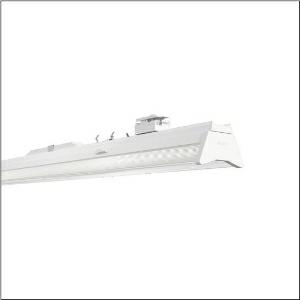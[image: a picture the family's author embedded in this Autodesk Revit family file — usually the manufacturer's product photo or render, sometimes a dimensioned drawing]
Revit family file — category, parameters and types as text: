
# Revit family: licross_r__21_performance_mo_51td16vn445g_3318
name_source: partatom
category: Lighting Fixtures
units: mm (PartAtom-declared; Revit-internal decimal feet)

## family parameters
Cut with Voids When Loaded = No
Host = Face
Light Source = No
Part Type = Normal
Room Calculation Point = No
Round Connector Dimension = Use Diameter
Shared = No

## types (1)
- --- (1 x LED, 4500 lm, 24.2 W, 4000K)
    Apparent Load = 24 VA
    CIE Flux Codes = 66 88 96 79 100
    Color Rendering = 80
    Color Temperature = 4000K
    Default Elevation = 1800 mm
    Description = Licross® 21 Performance MO, luminaire insert, of sheet steel, galvanised, coil coated, white, length: 1.500mm, width: 120mm, height: 123mm, LED rated luminous flux: 4.500lm, light colour: 840, control gear: DALI 2, CLO, with plug, 5-pole, with phase selection, mains connection: 220..240V, AC, 50/60Hz, start of lifetime: 24W, end of service life: 26W, internal wiring halogen-free, primary light control with lens, of plastic, primary optical cover: cover, of PMMA, light emission: direct/indirect distribution, primary light characteristic: symmetric, protection rating (complete): IP54, insulation class (complete): insulation class I (protective earthing), certification: CE, ENEC, VDE, UKCA, protection symbol: D if used in an environment with non-conductive dust loads with corresponding accessories, impact resistance: IK06, permissible ambient temperature for indoor applications: -25..+45°C, corresponds to IFS (International Featured Standards) requirements for safety and quality in the food industry, reducing of maximum allowable ambient temperature of 5°C with ceiling mounting, LABS conformity tested according to VDMA 24364:2018-05, packaging unit: 1 piece
    Height = 114 mm
    Lamp = 1 x LED
    Lamp Light Flux = 4500 lm
    Lamp Power = 24.2 W
    Lamp count = 1
    Length = 1500 mm
    Luminous efficacy = 186 lm/W
    Manufacturer = Siteco
    ModVariant = No
    Model = 51TD16VN445G
    Mounting Place = Ceiling
    Mounting Type = Pendant
    Number of Poles = 1
    OnlyDefault = Yes
    Power Factor = 1
    Product Name = Licross® 21 Performance MO
    Product group = luminaire insert | ceiling pendant
    ProductGroupID = 902
    Protection Class = Protection class I
    Protection Degree = IP 54
    RLX_Detail_Level = 1
    RLX_Emergency_Light_Flux = 0 lm
    RLX_Emergency_Type = 0
    RLX_Emergency_Type_DB = No
    RlxData = <blob elided: 33797 chars, md5=fe917436>
    Socket = socket
    Standby Power = 0 W
    System Light Flux = 4500 lm
    System Power = 24 W
    Type Comments = factory setting: luminous flux: 100 % | dim-lin: 254 | 160 mA
    Type Image = l_1256138.jpg
    URL = http://relux.com
    VarID = @adj_070009
    Voltage = 0 V
    Weight = 0.00 kg
    Width = 120 mm

## geometry (parser evidence)
native form markers: Blend x4, Sweep x10
no freeform markers — native parametric forms only
